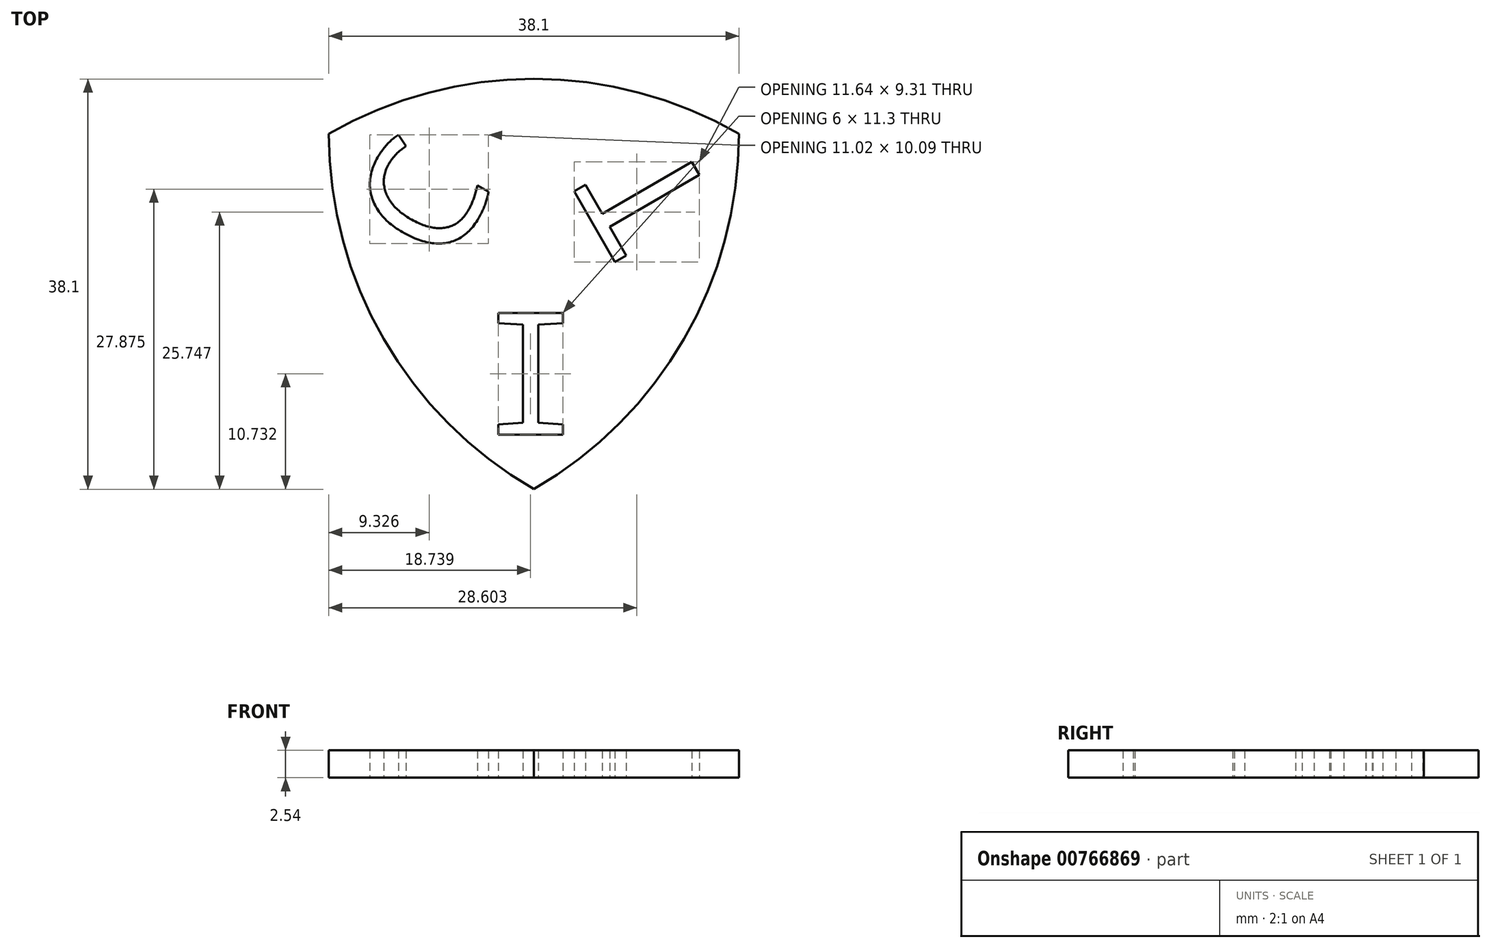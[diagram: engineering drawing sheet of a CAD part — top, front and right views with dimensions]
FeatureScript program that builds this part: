
annotation { "Feature Type Name" : "Feature", "Feature Type Description" : "" }
export const myFeature = defineFeature(function(context is Context, id is Id, definition is map)
    precondition{}
    {
        {
            var Q0;
            Q0=qCreatedBy(makeId("Top.planeOp"),FACE);
            var sketch = newSketch(context, id + "F0", { "sketchPlane" : qUnion([Q0])});
            skCircle(sketch, "E0", {"center": v(0, 0) * mm, "radius": 38.1 * mm});
            skSolve(sketch);
        }
        {
            var Q0;
            Q0=qCreatedBy(makeId("Top.planeOp"),FACE);
            var sketch = newSketch(context, id + "F1", { "sketchPlane" : qUnion([Q0])});
            skCircle(sketch, "E1", {"center": v(-38.1, 0) * mm, "radius": 38.1 * mm});
            skSolve(sketch);
        }
        {
            var Q0;
            Q0=qCreatedBy(makeId("Top.planeOp"),FACE);
            var sketch = newSketch(context, id + "F2", { "sketchPlane" : qUnion([Q0])});
            skCircle(sketch, "E2", {"center": v(-19.05, -33) * mm, "radius": 38.1 * mm});
            skSolve(sketch);
        }
        {
            var Q0;
            Q0 = qSketchRegion(id + "F0", true);
            extrude(context, id + "F3", {"entities" : qUnion([Q0]), "depth" : 2.54 * mm, "offsetDistance" : 25.4 * mm});
        }
        {
            var Q0;
            Q0=makeQuery(id+"F1.imprint","IMPRINT",FACE,{"disambiguationData":[TD([[makeQuery(id+"F1.imprint","IMPRINT",EDGE,{"derivedFrom":sQuery(id+"F1.wireOp",EDGE,"E1")}),1.0]])]});
            extrude(context, id + "F4", {"entities" : qUnion([Q0]), "depth" : 2.54 * mm, "offsetDistance" : 25.4 * mm});
        }
        {
            var Q0;
            Q0=makeQuery(id+"F2.imprint","IMPRINT",FACE,{"disambiguationData":[TD([[makeQuery(id+"F2.imprint","IMPRINT",EDGE,{"derivedFrom":sQuery(id+"F2.wireOp",EDGE,"E2")}),1.0]])]});
            extrude(context, id + "F5", {"entities" : qUnion([Q0]), "depth" : 2.54 * mm, "offsetDistance" : 25.4 * mm});
        }
        {
            var Q0;
            Q0=makeQuery(id+"F3.opExtrude","SWEPT_BODY",BODY,{"disambiguationData":[OSD([sQuery(id+"F0.wireOp",EDGE,"E0")])]});
            var Q1;
            Q1=makeQuery(id+"F4.opExtrude","SWEPT_BODY",BODY,{"disambiguationData":[OSD([sQuery(id+"F1.wireOp",EDGE,"E1")])]});
            var Q2;
            Q2=makeQuery(id+"F5.opExtrude","SWEPT_BODY",BODY,{"disambiguationData":[OSD([sQuery(id+"F2.wireOp",EDGE,"E2")])]});
            booleanBodies(context, id + "F6", {"operationType" : BooleanOperationType.INTERSECTION, "tools" : qUnion([Q0, Q1, Q2])});
        }
        {
            var Q0;
            Q0=qCreatedBy(makeId("Top.planeOp"),FACE);
            var sketch = newSketch(context, id + "F7", { "sketchPlane" : qUnion([Q0])});
            skText(sketch, "E3", { "text": "C", "fontName": "DroidSansMono.ttf"});
            skText(sketch, "E4", { "text": "I", "fontName": "DroidSansMono.ttf"});
            skText(sketch, "E5", { "text": "T", "fontName": "DroidSansMono.ttf"});
            const initialGuessF7  = {"E3": [-0.02711, -0.0126, 0.5, 0.86603, 0.01073], "E4": [-0.0241, -0.02792, 1, 0, 0.0114], "E5": [-0.00175, -0.00714, -0.5, 0.86603, 0.01094]};
            skSetInitialGuess(sketch, initialGuessF7);
            skSolve(sketch);
        }
        {
            var Q0;
            Q0 = qSketchRegion(id + "F7", true);
            extrude(context, id + "F8", {"entities" : qUnion([Q0]), "depth" : 2.54 * mm, "offsetDistance" : 25.4 * mm});
        }
        {
            var Q0;
            Q0=makeQuery(id+"F8.opExtrude","SWEPT_BODY",BODY,{"disambiguationData":[OSD([sQuery(id+"F7.wireOp",EDGE,"E5.sketch_text.stroke-0"),sQuery(id+"F7.wireOp",EDGE,"E5.sketch_text.stroke-1"),sQuery(id+"F7.wireOp",EDGE,"E5.sketch_text.stroke-2"),sQuery(id+"F7.wireOp",EDGE,"E5.sketch_text.stroke-3"),sQuery(id+"F7.wireOp",EDGE,"E5.sketch_text.stroke-4"),sQuery(id+"F7.wireOp",EDGE,"E5.sketch_text.stroke-5"),sQuery(id+"F7.wireOp",EDGE,"E5.sketch_text.stroke-6"),sQuery(id+"F7.wireOp",EDGE,"E5.sketch_text.stroke-7")])]});
            var Q1;
            Q1=makeQuery(id+"F8.opExtrude","SWEPT_BODY",BODY,{"disambiguationData":[OSD([sQuery(id+"F7.wireOp",EDGE,"E4.sketch_text.stroke-0"),sQuery(id+"F7.wireOp",EDGE,"E4.sketch_text.stroke-1"),sQuery(id+"F7.wireOp",EDGE,"E4.sketch_text.stroke-2"),sQuery(id+"F7.wireOp",EDGE,"E4.sketch_text.stroke-3"),sQuery(id+"F7.wireOp",EDGE,"E4.sketch_text.stroke-4"),sQuery(id+"F7.wireOp",EDGE,"E4.sketch_text.stroke-5"),sQuery(id+"F7.wireOp",EDGE,"E4.sketch_text.stroke-6"),sQuery(id+"F7.wireOp",EDGE,"E4.sketch_text.stroke-7"),sQuery(id+"F7.wireOp",EDGE,"E4.sketch_text.stroke-8"),sQuery(id+"F7.wireOp",EDGE,"E4.sketch_text.stroke-9"),sQuery(id+"F7.wireOp",EDGE,"E4.sketch_text.stroke-10"),sQuery(id+"F7.wireOp",EDGE,"E4.sketch_text.stroke-11")])]});
            var Q2;
            Q2=makeQuery(id+"F8.opExtrude","SWEPT_BODY",BODY,{"disambiguationData":[OSD([sQuery(id+"F7.wireOp",EDGE,"E3.sketch_text.stroke-0"),sQuery(id+"F7.wireOp",EDGE,"E3.sketch_text.stroke-1"),sQuery(id+"F7.wireOp",EDGE,"E3.sketch_text.stroke-2"),sQuery(id+"F7.wireOp",EDGE,"E3.sketch_text.stroke-3"),sQuery(id+"F7.wireOp",EDGE,"E3.sketch_text.stroke-4"),sQuery(id+"F7.wireOp",EDGE,"E3.sketch_text.stroke-5"),sQuery(id+"F7.wireOp",EDGE,"E3.sketch_text.stroke-6"),sQuery(id+"F7.wireOp",EDGE,"E3.sketch_text.stroke-7"),sQuery(id+"F7.wireOp",EDGE,"E3.sketch_text.stroke-8"),sQuery(id+"F7.wireOp",EDGE,"E3.sketch_text.stroke-9"),sQuery(id+"F7.wireOp",EDGE,"E3.sketch_text.stroke-10"),sQuery(id+"F7.wireOp",EDGE,"E3.sketch_text.stroke-11"),sQuery(id+"F7.wireOp",EDGE,"E3.sketch_text.stroke-12"),sQuery(id+"F7.wireOp",EDGE,"E3.sketch_text.stroke-13")])]});
            var Q3;
            Q3=makeQuery(id+"F6.opBoolean","INTERSECT",BODY,{"derivedFrom":[makeQuery(id+"F3.opExtrude","SWEPT_BODY",BODY,{"disambiguationData":[OSD([sQuery(id+"F0.wireOp",EDGE,"E0")])]}),makeQuery(id+"F4.opExtrude","SWEPT_BODY",BODY,{"disambiguationData":[OSD([sQuery(id+"F1.wireOp",EDGE,"E1")])]}),makeQuery(id+"F5.opExtrude","SWEPT_BODY",BODY,{"disambiguationData":[OSD([sQuery(id+"F2.wireOp",EDGE,"E2")])]})]});
            booleanBodies(context, id + "F9", {"operationType" : BooleanOperationType.SUBTRACTION, "tools" : qUnion([Q0, Q1, Q2]), "targets" : qUnion([Q3])});
        }
    });
